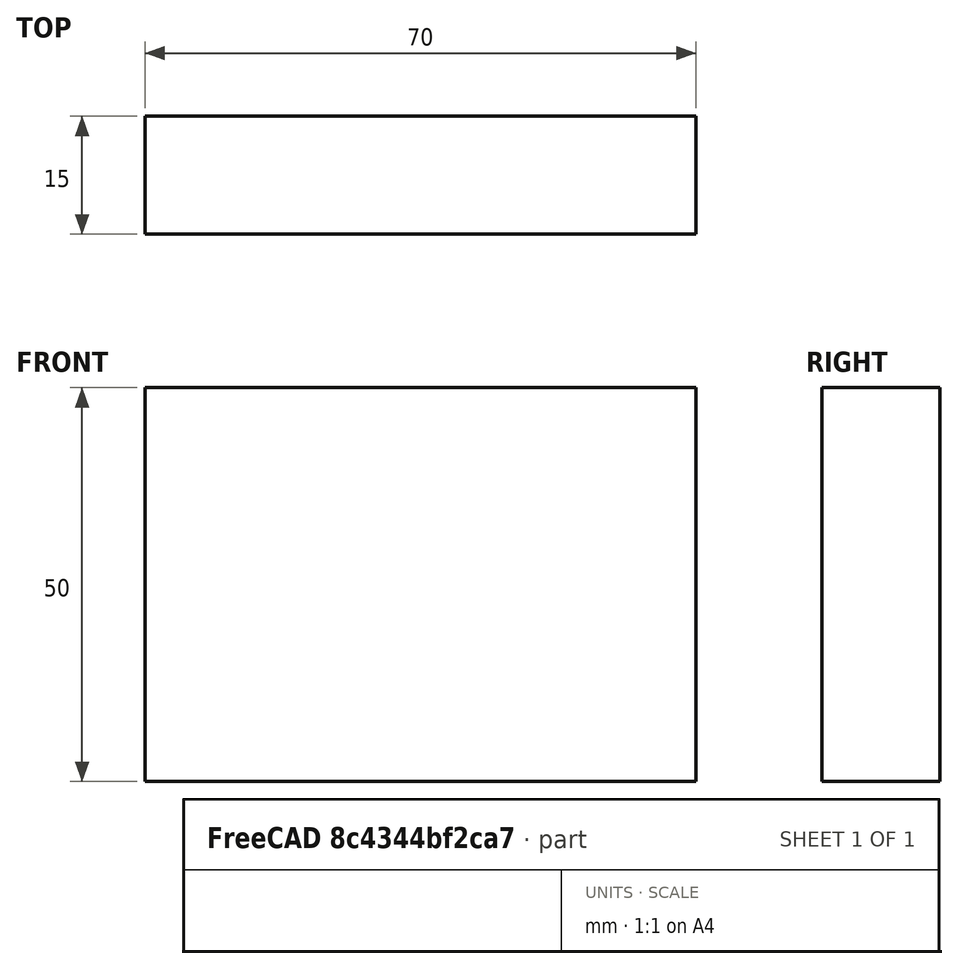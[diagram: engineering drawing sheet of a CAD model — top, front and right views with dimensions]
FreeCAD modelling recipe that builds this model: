
FCSTD DOCUMENT  (FreeCAD 0.15R4671 (Git))
Label: Flat Bar 70x15 EN10058 S235JR
License: All rights reserved
LicenseURL: http://en.wikipedia.org/wiki/All_rights_reserved
objects: Sketcher::SketchObject×1, Part::Extrusion×1
note: 2 computed .brp shape members not serialized (recipe doc carries the construction recipe); baked Part::Feature solids carry a one-line shape summary decoded from their .brp

FEATURE [Sketcher::SketchObject] Sketch
  sketch-geometry (4):
    g0: LineSegment StartX=-35 StartY=-7.5 StartZ=0 EndX=35 EndY=-7.5 EndZ=0
    g1: LineSegment StartX=35 StartY=-7.5 StartZ=0 EndX=35 EndY=7.5 EndZ=0
    g2: LineSegment StartX=35 StartY=7.5 StartZ=0 EndX=-35 EndY=7.5 EndZ=0
    g3: LineSegment StartX=-35 StartY=7.5 StartZ=0 EndX=-35 EndY=-7.5 EndZ=0
  constraints (12):
    c: Coincident(g0,g1)
    c: Coincident(g1,g2)
    c: Coincident(g2,g3)
    c: Coincident(g3,g0)
    c: Horizontal(g0)
    c: Horizontal(g2)
    c: Vertical(g1)
    c: Vertical(g3)
    c: Symmetric(g1,g2,g-2)
    c: Symmetric(g0,g1,g-1)
    c: DistanceY(g1) = 15
    c: DistanceX(g0) = 70
FEATURE [Part::Extrusion] Extrude  label="Flat Bar 70x15 EN10058 S235JR"
  Base = -> Sketch
  Dir = (0,0,50)
  Solid = true
